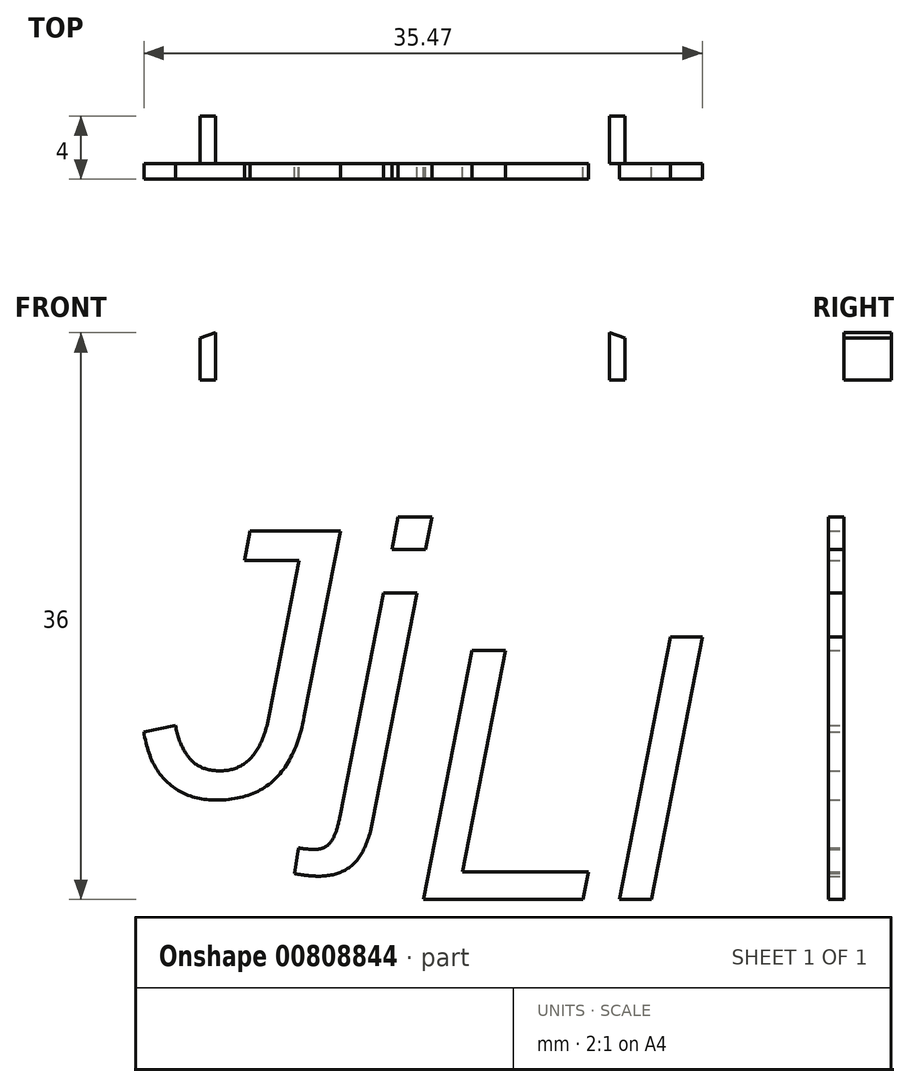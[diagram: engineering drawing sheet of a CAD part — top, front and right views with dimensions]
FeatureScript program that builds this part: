
annotation { "Feature Type Name" : "Feature", "Feature Type Description" : "" }
export const myFeature = defineFeature(function(context is Context, id is Id, definition is map)
    precondition{}
    {
        {
            var Q0;
            Q0=qCreatedBy(makeId("Front.planeOp"),FACE);
            var sketch = newSketch(context, id + "F0", { "sketchPlane" : qUnion([Q0])});
            skLineSegment(sketch, "E0.bottom", {"start": v(-35.5, 39) * mm, "end": v(35.5, 39) * mm});
            skLineSegment(sketch, "E0.top", {"start": v(-35.5, -39) * mm, "end": v(35.5, -39) * mm});
            skLineSegment(sketch, "E0.left", {"start": v(-35.5, 39) * mm, "end": v(-35.5, -39) * mm});
            skLineSegment(sketch, "E0.right", {"start": v(35.5, 39) * mm, "end": v(35.5, -39) * mm});
            skPoint(sketch, "E0.middle", {"position": v(0, 0) * mm});
            skLineSegment(sketch, "E1.top", {"start": v(-35.5, 31) * mm, "end": v(35.5, 31) * mm});
            skLineSegment(sketch, "E1.left", {"start": v(-35.5, -39) * mm, "end": v(-35.5, 31) * mm});
            skLineSegment(sketch, "E1.right", {"start": v(35.5, -39) * mm, "end": v(35.5, 31) * mm});
            skLineSegment(sketch, "E2.bottom", {"start": v(-12.5, 39) * mm, "end": v(12.5, 39) * mm});
            skLineSegment(sketch, "E2.top", {"start": v(-12.5, 31) * mm, "end": v(12.5, 31) * mm});
            skLineSegment(sketch, "E2.left", {"start": v(-12.5, 39) * mm, "end": v(-12.5, 31) * mm});
            skLineSegment(sketch, "E2.right", {"start": v(12.5, 39) * mm, "end": v(12.5, 31) * mm});
            skLineSegment(sketch, "E3", {"start": v(-35.5, 31) * mm, "end": v(-12.5, 39) * mm});
            skLineSegment(sketch, "E4", {"start": v(12.5, 39) * mm, "end": v(35.5, 31) * mm});
            skLineSegment(sketch, "E5.bottom", {"start": v(-32.5, -10) * mm, "end": v(-38.5, -10) * mm});
            skLineSegment(sketch, "E5.top", {"start": v(-32.5, 10) * mm, "end": v(-38.5, 10) * mm});
            skLineSegment(sketch, "E5.left", {"start": v(-32.5, -10) * mm, "end": v(-32.5, 10) * mm});
            skLineSegment(sketch, "E5.right", {"start": v(-38.5, -10) * mm, "end": v(-38.5, 10) * mm});
            skPoint(sketch, "E5.middle", {"position": v(-35.5, 0) * mm});
            skLineSegment(sketch, "E6.bottom", {"start": v(32.5, -10) * mm, "end": v(38.5, -10) * mm});
            skLineSegment(sketch, "E6.top", {"start": v(32.5, 10) * mm, "end": v(38.5, 10) * mm});
            skLineSegment(sketch, "E6.left", {"start": v(32.5, -10) * mm, "end": v(32.5, 10) * mm});
            skLineSegment(sketch, "E6.right", {"start": v(38.5, -10) * mm, "end": v(38.5, 10) * mm});
            skPoint(sketch, "E6.middle", {"position": v(35.5, 0) * mm});
            skLineSegment(sketch, "E7.bottom", {"start": v(-10, -42) * mm, "end": v(10, -42) * mm});
            skLineSegment(sketch, "E7.top", {"start": v(-10, -36) * mm, "end": v(10, -36) * mm});
            skLineSegment(sketch, "E7.left", {"start": v(-10, -42) * mm, "end": v(-10, -36) * mm});
            skLineSegment(sketch, "E7.right", {"start": v(10, -42) * mm, "end": v(10, -36) * mm});
            skPoint(sketch, "E7.middle", {"position": v(0, -39) * mm});
            skLineSegment(sketch, "E8.bottom", {"start": v(-12.5, 39) * mm, "end": v(-13.5, 39) * mm});
            skLineSegment(sketch, "E8.top", {"start": v(-12.5, 36) * mm, "end": v(-13.5, 36) * mm});
            skLineSegment(sketch, "E8.left", {"start": v(-12.5, 39) * mm, "end": v(-12.5, 36) * mm});
            skLineSegment(sketch, "E8.right", {"start": v(-13.5, 39) * mm, "end": v(-13.5, 36) * mm});
            skLineSegment(sketch, "E9.bottom", {"start": v(12.5, 39) * mm, "end": v(13.5, 39) * mm});
            skLineSegment(sketch, "E9.top", {"start": v(12.5, 36) * mm, "end": v(13.5, 36) * mm});
            skLineSegment(sketch, "E9.left", {"start": v(12.5, 39) * mm, "end": v(12.5, 36) * mm});
            skLineSegment(sketch, "E9.right", {"start": v(13.5, 39) * mm, "end": v(13.5, 36) * mm});
            skSolve(sketch);
        }
        {
            var Q0;
            {var subQ0=sQuery(id+"F0.wireOp",EDGE,"E2.top");Q0=makeQuery(id+"F0.imprint","IMPRINT",FACE,{"disambiguationData":[TD([[makeQuery(id+"F0.imprint","IMPRINT",EDGE,{"derivedFrom":subQ0}),-1.0]])]});}
            var Q1;
            {var subQ6=sQuery(id+"F0.wireOp",EDGE,"E2.left");Q1=makeQuery(id+"F0.imprint","IMPRINT",FACE,{"disambiguationData":[TD([[makeQuery(id+"F0.imprint","IMPRINT",EDGE,{"derivedFrom":subQ6}),-1.0]])]});}
            var Q2;
            {var subQ6=sQuery(id+"F0.wireOp",EDGE,"E2.right");Q2=makeQuery(id+"F0.imprint","IMPRINT",FACE,{"disambiguationData":[TD([[makeQuery(id+"F0.imprint","IMPRINT",EDGE,{"derivedFrom":subQ6}),1.0]])]});}
            extrude(context, id + "F1", {"entities" : qUnion([Q0, Q1, Q2]), "depth" : 3 * mm, "offsetDistance" : 25 * mm});
        }
        {
            var Q0;
            Q0=makeQuery(id+"F1.opExtrude","CAP_FACE",FACE,{"disambiguationData":[OSD([sQuery(id+"F0.wireOp",EDGE,"E0.top"),sQuery(id+"F0.wireOp",EDGE,"E1.left"),sQuery(id+"F0.wireOp",EDGE,"E1.right"),sQuery(id+"F0.wireOp",EDGE,"E2.top"),sQuery(id+"F0.wireOp",EDGE,"E2.left"),sQuery(id+"F0.wireOp",EDGE,"E2.right"),sQuery(id+"F0.wireOp",EDGE,"E3"),sQuery(id+"F0.wireOp",EDGE,"E4"),sQuery(id+"F0.wireOp",EDGE,"E5.bottom"),sQuery(id+"F0.wireOp",EDGE,"E5.top"),sQuery(id+"F0.wireOp",EDGE,"E5.left"),sQuery(id+"F0.wireOp",EDGE,"E6.bottom"),sQuery(id+"F0.wireOp",EDGE,"E6.top"),sQuery(id+"F0.wireOp",EDGE,"E6.left"),sQuery(id+"F0.wireOp",EDGE,"E7.top"),sQuery(id+"F0.wireOp",EDGE,"E7.left"),sQuery(id+"F0.wireOp",EDGE,"E7.right"),sQuery(id+"F0.wireOp",EDGE,"E8.top"),sQuery(id+"F0.wireOp",EDGE,"E8.right"),sQuery(id+"F0.wireOp",EDGE,"E9.top"),sQuery(id+"F0.wireOp",EDGE,"E9.right")])],"isStart":false});
            var sketch = newSketch(context, id + "F2", { "sketchPlane" : qUnion([Q0])});
            skText(sketch, "E10", { "text": "Jj", "fontName": "Arimo-Italic.ttf"});
            skText(sketch, "E11", { "text": "Ll", "fontName": "Arimo-Italic.ttf"});
            const initialGuessF2  = {"E10": [-0.017, 0.00955, 1, 0, 0.01762], "E11": [0, 0.003, 1, 0, 0.01655]};
            skSetInitialGuess(sketch, initialGuessF2);
            skSolve(sketch);
        }
        {
            var Q0;
            Q0=qSketchRegion(id+"F2",true);
            extrude(context, id + "F3", {"entities" : qUnion([Q0]), "operationType" : NewBodyOperationType.ADD, "depth" : 1 * mm, "offsetDistance" : 25 * mm});
        }
    });
